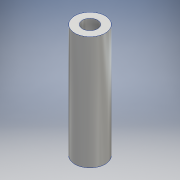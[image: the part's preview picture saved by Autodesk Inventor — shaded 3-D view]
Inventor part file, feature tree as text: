
AUTODESK INVENTOR PART (.ipt)
format: ipt  version: 2016 (Build 200138000, 138)  size: 107,520 bytes
history: native  units: mm
features: sketch x2, extrude x2, hole x2, other x1
ambient origin geometry x8: Origin, YZ Plane, XZ Plane, XY Plane, X Axis, Y Axis, Z Axis, Center Point
bodies: Body1 (feature_tree)
feature tree (7):
  other  "ソリッド1"
  sketch  "スケッチ1"
  extrude  "押し出し1"  Depth=8.0mm
  sketch  "スケッチ2"
  extrude  "押し出し2"  Depth=4.001mm
  hole  "穴1"  [1 undecoded]
  hole  "穴2"  [1 undecoded]
note: 2 required parameter values undecoded (feature->parameter linkage not recoverable at this tier; creation-order binding heuristic only, values carry confidence <= 0.55)
